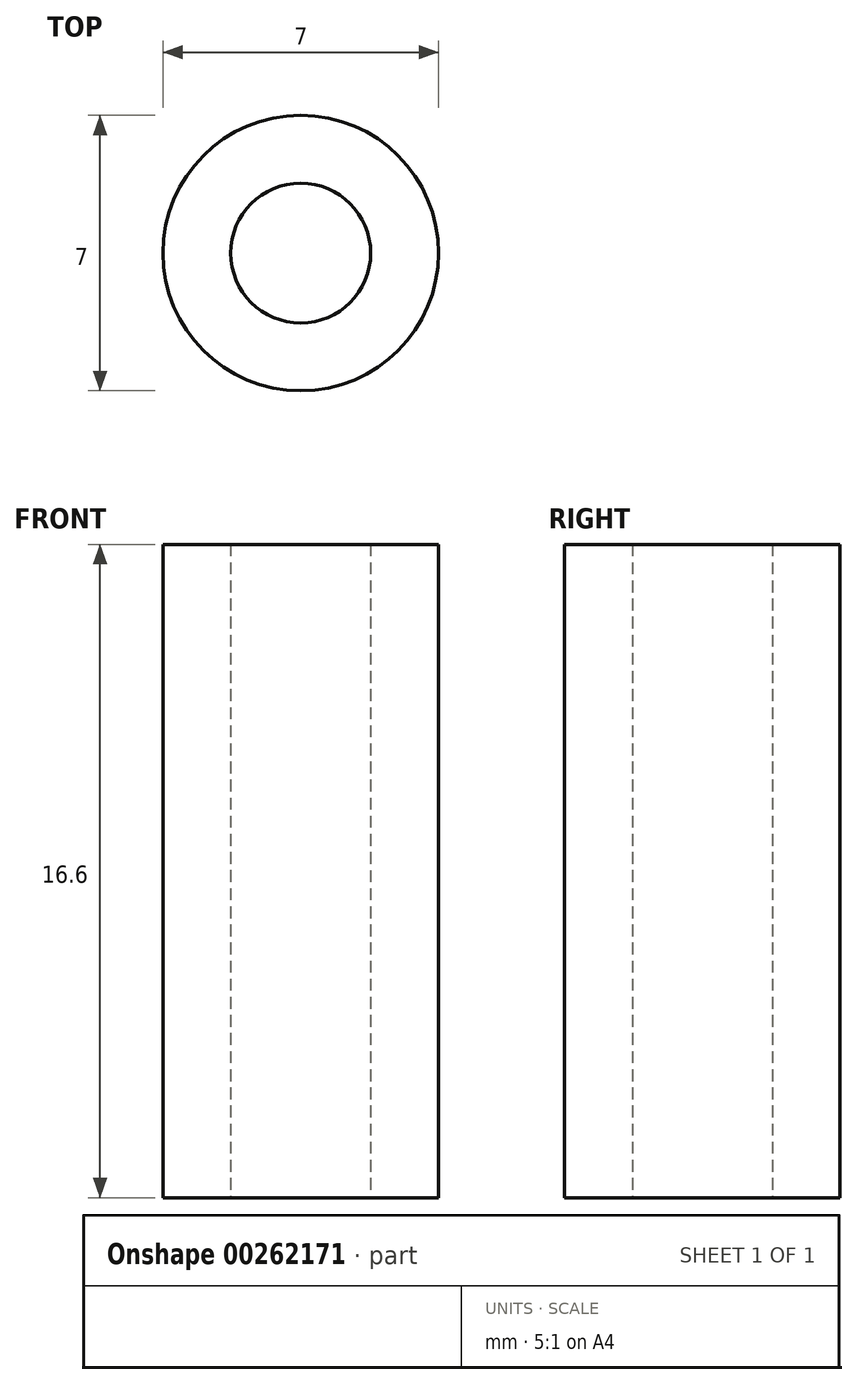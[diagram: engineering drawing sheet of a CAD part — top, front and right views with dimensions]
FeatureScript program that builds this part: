
annotation { "Feature Type Name" : "Feature", "Feature Type Description" : "" }
export const myFeature = defineFeature(function(context is Context, id is Id, definition is map)
    precondition{}
    {
        {
            var Q0;
            Q0=qCreatedBy(makeId("Top.planeOp"),FACE);
            var sketch = newSketch(context, id + "F0", { "sketchPlane" : qUnion([Q0])});
            skCircle(sketch, "E0", {"center": v(0, 0) * mm, "radius": 1.78 * mm});
            skCircle(sketch, "E1", {"center": v(0, 0) * mm, "radius": 3.5 * mm});
            skSolve(sketch);
        }
        {
            var Q0;
            Q0=makeQuery(id+"F0.imprint","IMPRINT",FACE,{"disambiguationData":[TD([[makeQuery(id+"F0.imprint","IMPRINT",EDGE,{"derivedFrom":sQuery(id+"F0.wireOp",EDGE,"E0")}),-1.0]])]});
            extrude(context, id + "F1", {"entities" : qUnion([Q0]), "depth" : 16.6 * mm});
        }
    });
